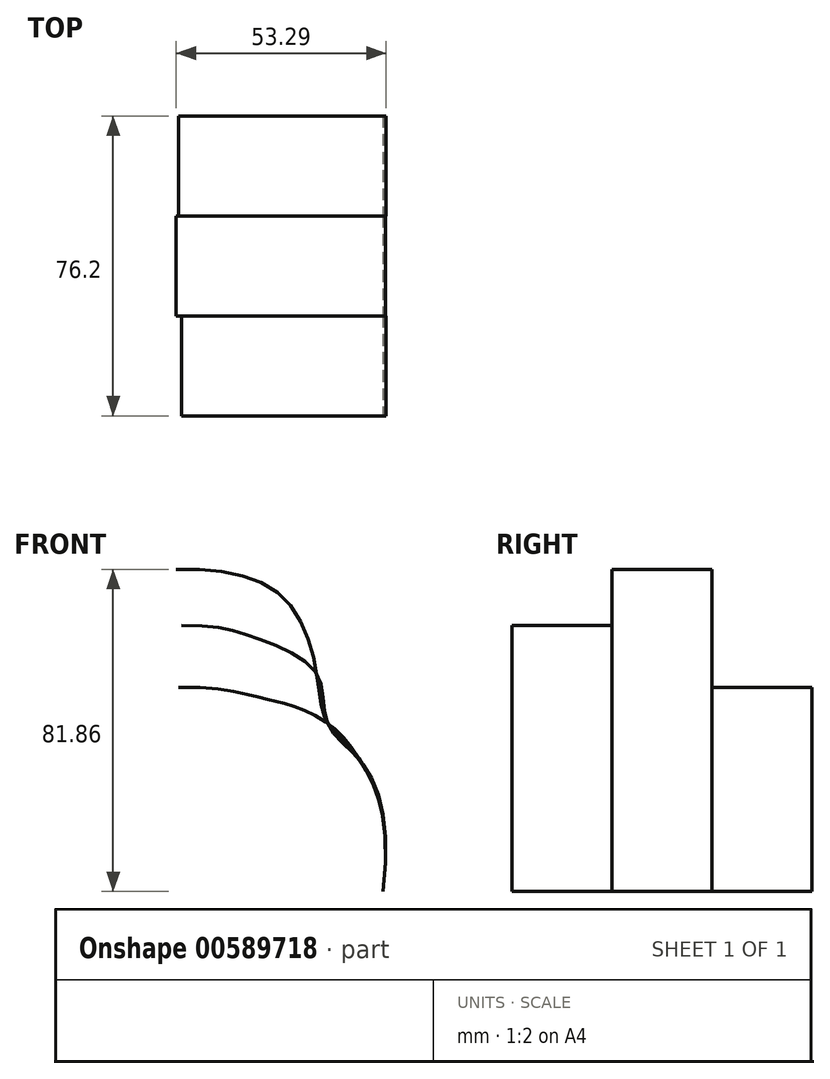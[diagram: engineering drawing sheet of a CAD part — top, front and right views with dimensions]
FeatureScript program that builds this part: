
annotation { "Feature Type Name" : "Feature", "Feature Type Description" : "" }
export const myFeature = defineFeature(function(context is Context, id is Id, definition is map)
    precondition{}
    {
        {
            var Q0;
            Q0=qCreatedBy(makeId("Front.planeOp"),FACE);
            cPlane(context, id + "F0", {"entities" : qUnion([Q0]), "cplaneType" : CPlaneType.OFFSET, "offset" : 25.4 * mm, "width" : 152.4 * mm, "height" : 152.4 * mm});
        }
        {
            var Q0;
            Q0=qCreatedBy(makeId("Front.planeOp"),FACE);
            cPlane(context, id + "F1", {"entities" : qUnion([Q0]), "cplaneType" : CPlaneType.OFFSET, "offset" : 50.8 * mm, "width" : 152.4 * mm, "height" : 152.4 * mm});
        }
        {
            var Q0;
            Q0=qCreatedBy(id+"F1.planeOp",FACE);
            cPlane(context, id + "F2", {"entities" : qUnion([Q0]), "cplaneType" : CPlaneType.OFFSET, "offset" : 25.4 * mm, "width" : 152.4 * mm, "height" : 152.4 * mm});
        }
        {
            var Q0;
            Q0=qCreatedBy(id+"F2.planeOp",FACE);
            cPlane(context, id + "F3", {"entities" : qUnion([Q0]), "cplaneType" : CPlaneType.OFFSET, "offset" : 25.4 * mm, "width" : 152.4 * mm, "height" : 152.4 * mm});
        }
        {
            var Q0;
            Q0=qCreatedBy(id+"F1.planeOp",FACE);
            var sketch = newSketch(context, id + "F4", { "sketchPlane" : qUnion([Q0])});
            skFitSpline(sketch, "E0", {"points": [v(-30.79, 57.3) * mm, v(-4.17, 50.7) * mm, v(4.86, 30.84) * mm, v(7.56, 18.36) * mm, v(16.29, 8.28) * mm, v(21.7, -24.5) * mm], "startDerivative": vector(135.83, 3.97) * mm, "endDerivative": vector(-25.09, -179.2) * mm});
            skLineSegment(sketch, "E1", {"start": v(21.7, -24.5) * mm, "end": v(-30.79, -24.5) * mm});
            skSolve(sketch);
        }
        {
            var Q0;
            Q0=qCreatedBy(id+"F0.planeOp",FACE);
            var sketch = newSketch(context, id + "F5", { "sketchPlane" : qUnion([Q0])});
            skFitSpline(sketch, "E2", {"points": [v(-30.28, 27.33) * mm, v(-9.32, 24.7) * mm, v(-2.58, 23.01) * mm, v(7.56, 18.36) * mm, v(16.29, 8.28) * mm, v(21.7, -24.5) * mm], "startDerivative": vector(135.83, 3.97) * mm, "endDerivative": vector(-25.09, -179.2) * mm});
            skLineSegment(sketch, "E3", {"start": v(21.7, -24.5) * mm, "end": v(-30.79, -24.5) * mm});
            skSolve(sketch);
        }
        {
            var Q0;
            Q0=qCreatedBy(id+"F2.planeOp",FACE);
            var sketch = newSketch(context, id + "F6", { "sketchPlane" : qUnion([Q0])});
            skFitSpline(sketch, "E4", {"points": [v(-29.5, 43.07) * mm, v(-10.94, 40) * mm, v(4.86, 30.84) * mm, v(7.56, 18.36) * mm, v(16.29, 8.28) * mm, v(21.7, -24.5) * mm], "startDerivative": vector(135.83, 3.97) * mm, "endDerivative": vector(-25.09, -179.2) * mm});
            skLineSegment(sketch, "E5", {"start": v(21.7, -24.5) * mm, "end": v(-30.79, -24.5) * mm});
            skSolve(sketch);
        }
        {
            var Q0;
            Q0=qCreatedBy(id+"F3.planeOp",FACE);
            cPlane(context, id + "F7", {"entities" : qUnion([Q0]), "cplaneType" : CPlaneType.OFFSET, "offset" : 25.4 * mm, "width" : 152.4 * mm, "height" : 152.4 * mm});
        }
        {
            var Q0;
            Q0=sQuery(id+"F5.wireOp",EDGE,"E2");
            extrude(context, id + "F8", {"bodyType" : ToolBodyType.SURFACE, "surfaceEntities" : qUnion([Q0]), "depth" : 25.4 * mm, "offsetDistance" : 25.4 * mm});
        }
        {
            var Q0;
            Q0=sQuery(id+"F6.wireOp",EDGE,"E4");
            extrude(context, id + "F9", {"bodyType" : ToolBodyType.SURFACE, "surfaceEntities" : qUnion([Q0]), "depth" : 25.4 * mm, "offsetDistance" : 25.4 * mm});
        }
        {
            var Q0;
            Q0=sQuery(id+"F4.wireOp",EDGE,"E0");
            extrude(context, id + "F10", {"bodyType" : ToolBodyType.SURFACE, "surfaceEntities" : qUnion([Q0]), "depth" : 25.4 * mm, "offsetDistance" : 25.4 * mm});
        }
    });
